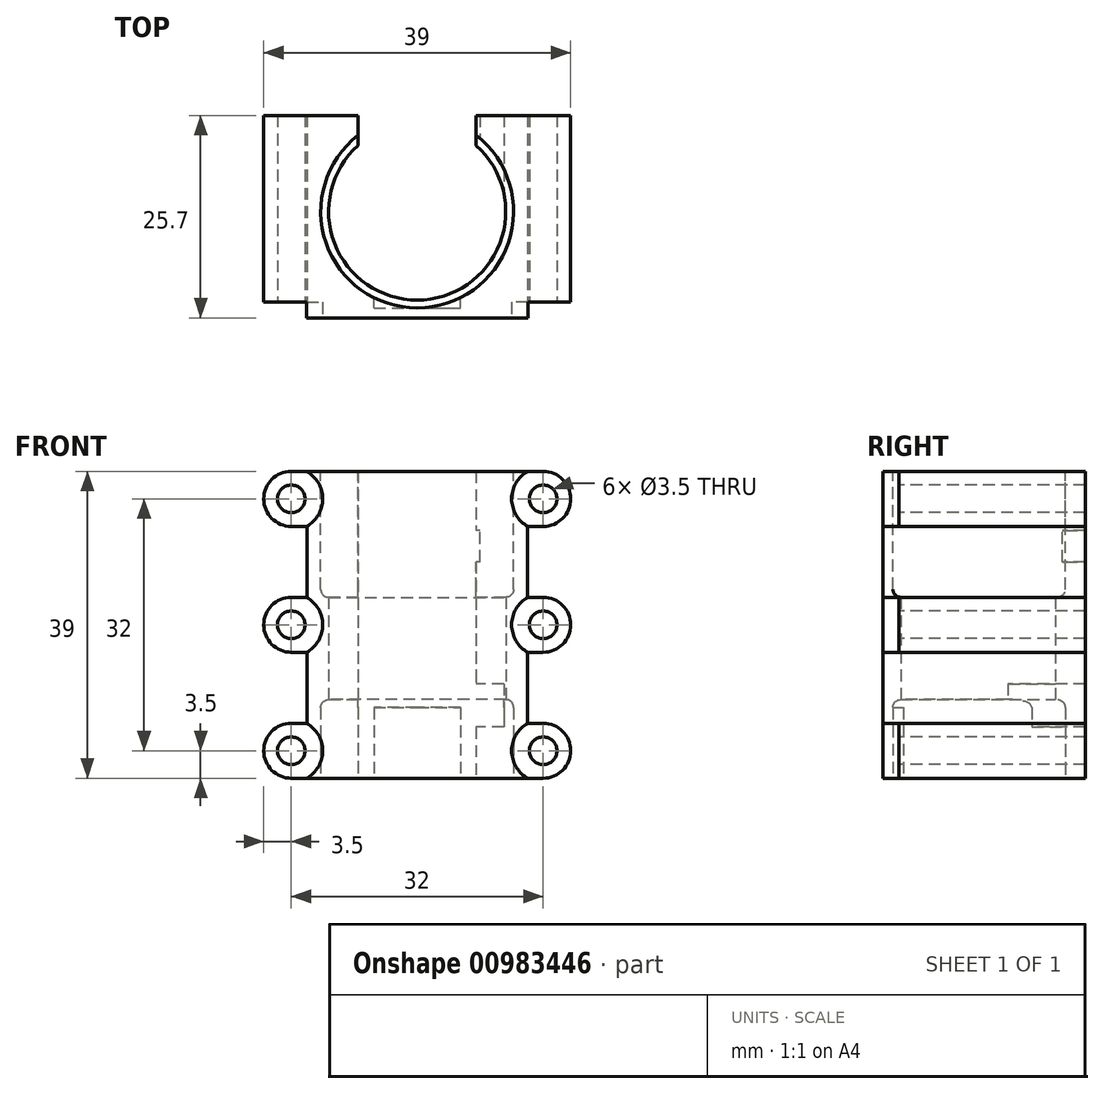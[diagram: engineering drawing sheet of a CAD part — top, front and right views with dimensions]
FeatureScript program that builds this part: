
annotation { "Feature Type Name" : "Feature", "Feature Type Description" : "" }
export const myFeature = defineFeature(function(context is Context, id is Id, definition is map)
    precondition{}
    {
        {
            var Q0;
            Q0=qCreatedBy(makeId("Top.planeOp"),FACE);
            var sketch = newSketch(context, id + "F0", { "sketchPlane" : qUnion([Q0])});
            skCircle(sketch, "E0", {"center": v(0, 0) * mm, "radius": 11.25 * mm});
            skSolve(sketch);
        }
        {
            var Q0;
            Q0=qSketchRegion(id+"F0",true);
            extrude(context, id + "F1", {"entities" : qUnion([Q0]), "depth" : 39 * mm, "offsetDistance" : 25 * mm});
        }
        {
            var Q0;
            Q0=makeQuery(id+"F1.opExtrude","CAP_FACE",FACE,{"disambiguationData":[OSD([sQuery(id+"F0.wireOp",EDGE,"E0")])],"isStart":false});
            var sketch = newSketch(context, id + "F2", { "sketchPlane" : qUnion([Q0])});
            skCircle(sketch, "E1", {"center": v(0, 0) * mm, "radius": 12.25 * mm});
            skSolve(sketch);
        }
        {
            var Q0;
            Q0=makeQuery(id+"F2.imprint","IMPRINT",FACE,{"disambiguationData":[TD([[makeQuery(id+"F2.imprint","IMPRINT",EDGE,{"derivedFrom":sQuery(id+"F2.wireOp",EDGE,"E1")}),1.0]])]});
            extrude(context, id + "F3", {"entities" : qUnion([Q0]), "operationType" : NewBodyOperationType.ADD, "oppositeDirection" : true, "depth" : 16 * mm, "offsetDistance" : 25 * mm});
        }
        {
            var Q0;
            Q0=makeQuery(id+"F1.opExtrude","CAP_FACE",FACE,{"disambiguationData":[OSD([sQuery(id+"F0.wireOp",EDGE,"E0")])],"isStart":true});
            var sketch = newSketch(context, id + "F4", { "sketchPlane" : qUnion([Q0])});
            skCircle(sketch, "E2", {"center": v(0, 0) * mm, "radius": 12.25 * mm});
            skSolve(sketch);
        }
        {
            var Q0;
            Q0=makeQuery(id+"F3.opExtrude","CAP_EDGE",EDGE,{"disambiguationData":[OSD([sQuery(id+"F2.wireOp",EDGE,"E1")])],"isStart":false});
            fillet(context, id + "F5", {"entities" : qUnion([Q0]), "radius" : 1 * mm, "tangentPropagation" : true, "allowEdgeOverflow" : false});
        }
        {
            var Q0;
            Q0=makeQuery(id+"F4.imprint","IMPRINT",FACE,{"disambiguationData":[TD([[makeQuery(id+"F4.imprint","IMPRINT",EDGE,{"derivedFrom":sQuery(id+"F4.wireOp",EDGE,"E2")}),1.0]])]});
            extrude(context, id + "F6", {"entities" : qUnion([Q0]), "operationType" : NewBodyOperationType.ADD, "oppositeDirection" : true, "depth" : 10 * mm, "offsetDistance" : 25 * mm});
        }
        {
            var Q0;
            Q0=makeQuery(id+"F6.opExtrude","CAP_EDGE",EDGE,{"disambiguationData":[OSD([sQuery(id+"F4.wireOp",EDGE,"E2")])],"isStart":false});
            fillet(context, id + "F7", {"entities" : qUnion([Q0]), "radius" : 1 * mm, "tangentPropagation" : true, "allowEdgeOverflow" : false});
        }
        {
            var Q0;
            {var subQ0=sQuery(id+"F0.wireOp",EDGE,"E0");Q0=makeQuery(id+"F6.boolean.opBoolean","MERGE",FACE,{"derivedFrom":[makeQuery(id+"F1.opExtrude","CAP_FACE",FACE,{"disambiguationData":[OSD([subQ0])],"isStart":true}),makeQuery(id+"F6.opExtrude","CAP_FACE",FACE,{"disambiguationData":[OSD([subQ0,sQuery(id+"F4.wireOp",EDGE,"E2")])],"isStart":true})]});}
            var sketch = newSketch(context, id + "F8", { "sketchPlane" : qUnion([Q0])});
            skLineSegment(sketch, "E3.bottom", {"start": v(-5.5, 12.25) * mm, "end": v(5.5, 12.25) * mm});
            skLineSegment(sketch, "E3.top", {"start": v(-5.5, 10.25) * mm, "end": v(5.5, 10.25) * mm});
            skLineSegment(sketch, "E3.left", {"start": v(-5.5, 12.25) * mm, "end": v(-5.5, 10.25) * mm});
            skLineSegment(sketch, "E3.right", {"start": v(5.5, 12.25) * mm, "end": v(5.5, 10.25) * mm});
            skPoint(sketch, "E3.middle", {"position": v(0, 11.25) * mm});
            skSolve(sketch);
        }
        {
            var Q0;
            {var subQ0=sQuery(id+"F8.wireOp",EDGE,"E3.left");var subQ1=sQuery(id+"F8.wireOp",EDGE,"E3.bottom");var subQ2=makeQuery(id+"F8.imprint","INTERSECT",VERTEX,{"derivedFrom":[subQ1,subQ0]});Q0=makeQuery(id+"F8.imprint","IMPRINT",FACE,{"disambiguationData":[TD([[makeQuery(id+"F8.imprint","IMPRINT",EDGE,{"disambiguationData":[TD([[subQ2,-1.0]])],"derivedFrom":subQ1}),-1.0]])]});}
            var Q1;
            {var subQ0=sQuery(id+"F8.wireOp",EDGE,"E3.right");var subQ1=sQuery(id+"F8.wireOp",EDGE,"E3.bottom");var subQ2=makeQuery(id+"F8.imprint","INTERSECT",VERTEX,{"derivedFrom":[subQ1,subQ0]});Q1=makeQuery(id+"F8.imprint","IMPRINT",FACE,{"disambiguationData":[TD([[makeQuery(id+"F8.imprint","IMPRINT",EDGE,{"disambiguationData":[TD([[subQ2,1.0]])],"derivedFrom":subQ1}),-1.0]])]});}
            extrude(context, id + "F9", {"entities" : qUnion([Q0, Q1]), "operationType" : NewBodyOperationType.ADD, "oppositeDirection" : true, "depth" : 9 * mm, "offsetDistance" : 25 * mm});
        }
        {
            var Q0;
            {var subQ0=sQuery(id+"F8.wireOp",EDGE,"E3.bottom");var subQ1=sQuery(id+"F4.wireOp",EDGE,"E2");var subQ2=sQuery(id+"F0.wireOp",EDGE,"E0");Q0=makeQuery(id+"F9.boolean.opBoolean","MERGE",FACE,{"derivedFrom":[makeQuery(id+"F6.boolean.opBoolean","MERGE",FACE,{"derivedFrom":[makeQuery(id+"F1.opExtrude","CAP_FACE",FACE,{"disambiguationData":[OSD([subQ2])],"isStart":true}),makeQuery(id+"F6.opExtrude","CAP_FACE",FACE,{"disambiguationData":[OSD([subQ2,subQ1])],"isStart":true})]}),makeQuery(id+"F9.opExtrude","CAP_FACE",FACE,{"disambiguationData":[OSD([subQ1,subQ0,sQuery(id+"F8.wireOp",EDGE,"E3.left")])],"isStart":true}),makeQuery(id+"F9.opExtrude","CAP_FACE",FACE,{"disambiguationData":[OSD([subQ1,subQ0,sQuery(id+"F8.wireOp",EDGE,"E3.right")])],"isStart":true})]});}
            var sketch = newSketch(context, id + "F10", { "sketchPlane" : qUnion([Q0])});
            skLineSegment(sketch, "E4.bottom", {"start": v(-7.5, -8.25) * mm, "end": v(7.5, -8.25) * mm});
            skLineSegment(sketch, "E4.top", {"start": v(-7.5, -12.25) * mm, "end": v(7.5, -12.25) * mm});
            skLineSegment(sketch, "E4.left", {"start": v(-7.5, -8.25) * mm, "end": v(-7.5, -12.25) * mm});
            skLineSegment(sketch, "E4.right", {"start": v(7.5, -8.25) * mm, "end": v(7.5, -12.25) * mm});
            skPoint(sketch, "E4.middle", {"position": v(0, -10.25) * mm});
            skSolve(sketch);
        }
        {
            var Q0;
            {var subQ0=sQuery(id+"F10.wireOp",EDGE,"E4.right");var subQ1=sQuery(id+"F10.wireOp",EDGE,"E4.top");var subQ2=makeQuery(id+"F10.imprint","INTERSECT",VERTEX,{"derivedFrom":[subQ1,subQ0]});Q0=makeQuery(id+"F10.imprint","IMPRINT",FACE,{"disambiguationData":[TD([[makeQuery(id+"F10.imprint","IMPRINT",EDGE,{"disambiguationData":[TD([[subQ2,1.0]])],"derivedFrom":subQ1}),1.0]])]});}
            var Q1;
            {var subQ0=sQuery(id+"F10.wireOp",EDGE,"E4.left");var subQ1=sQuery(id+"F10.wireOp",EDGE,"E4.top");var subQ2=makeQuery(id+"F10.imprint","INTERSECT",VERTEX,{"derivedFrom":[subQ1,subQ0]});Q1=makeQuery(id+"F10.imprint","IMPRINT",FACE,{"disambiguationData":[TD([[makeQuery(id+"F10.imprint","IMPRINT",EDGE,{"disambiguationData":[TD([[subQ2,-1.0]])],"derivedFrom":subQ1}),1.0]])]});}
            var Q2;
            {var subQ4=sQuery(id+"F10.wireOp",EDGE,"E4.bottom");Q2=makeQuery(id+"F10.imprint","IMPRINT",FACE,{"disambiguationData":[TD([[makeQuery(id+"F10.imprint","IMPRINT",EDGE,{"derivedFrom":subQ4}),-1.0]])]});}
            extrude(context, id + "F11", {"entities" : qUnion([Q0, Q1, Q2]), "operationType" : NewBodyOperationType.ADD, "oppositeDirection" : true, "depth" : 39 * mm, "offsetDistance" : 25 * mm});
        }
        {
            var Q0;
            Q0=makeQuery(id+"F11.opExtrude","SWEPT_FACE",FACE,{"disambiguationData":[OSD([sQuery(id+"F10.wireOp",EDGE,"E4.top")])]});
            var sketch = newSketch(context, id + "F12", { "sketchPlane" : qUnion([Q0])});
            skLineSegment(sketch, "E5.bottom", {"start": v(-11, 12) * mm, "end": v(-7.5, 12) * mm});
            skLineSegment(sketch, "E5.top", {"start": v(-11, 6.5) * mm, "end": v(-7.5, 6.5) * mm});
            skLineSegment(sketch, "E5.left", {"start": v(-11, 12) * mm, "end": v(-11, 6.5) * mm});
            skLineSegment(sketch, "E5.right", {"start": v(-7.5, 12) * mm, "end": v(-7.5, 6.5) * mm});
            skSolve(sketch);
        }
        {
            var Q0;
            Q0=makeQuery(id+"F12.imprint","IMPRINT",FACE,{"disambiguationData":[TD([[makeQuery(id+"F12.imprint","IMPRINT",EDGE,{"derivedFrom":sQuery(id+"F12.wireOp",EDGE,"E5.bottom")}),-1.0]])]});
            extrude(context, id + "F13", {"entities" : qUnion([Q0]), "operationType" : NewBodyOperationType.ADD, "depth" : 2 * mm, "offsetDistance" : 25 * mm, "hasSecondDirection" : true, "secondDirectionOppositeDirection" : true, "secondDirectionDepth" : 12 * mm});
        }
        {
            var Q0;
            Q0=makeQuery(id+"F11.opExtrude","SWEPT_FACE",FACE,{"disambiguationData":[OSD([sQuery(id+"F10.wireOp",EDGE,"E4.top")])]});
            var sketch = newSketch(context, id + "F14", { "sketchPlane" : qUnion([Q0])});
            skCircle(sketch, "E6", {"center": v(-0.06, 19) * mm, "radius": 6.5 * mm});
            skSolve(sketch);
        }
        {
            var Q0;
            Q0=makeQuery(id+"F14.imprint","IMPRINT",FACE,{"disambiguationData":[TD([[makeQuery(id+"F14.imprint","IMPRINT",EDGE,{"derivedFrom":sQuery(id+"F14.wireOp",EDGE,"E6")}),1.0]])]});
            extrude(context, id + "F15", {"entities" : qUnion([Q0]), "operationType" : NewBodyOperationType.ADD, "depth" : 2 * mm, "offsetDistance" : 25 * mm});
        }
        {
            var Q0;
            Q0=makeQuery(id+"F11.opExtrude","SWEPT_FACE",FACE,{"disambiguationData":[OSD([sQuery(id+"F10.wireOp",EDGE,"E4.top")])]});
            var sketch = newSketch(context, id + "F16", { "sketchPlane" : qUnion([Q0])});
            skLineSegment(sketch, "E7.bottom", {"start": v(-8, 27.5) * mm, "end": v(-4.5, 27.5) * mm});
            skLineSegment(sketch, "E7.top", {"start": v(-8, 31.5) * mm, "end": v(-4.5, 31.5) * mm});
            skLineSegment(sketch, "E7.left", {"start": v(-8, 27.5) * mm, "end": v(-8, 31.5) * mm});
            skLineSegment(sketch, "E7.right", {"start": v(-4.5, 27.5) * mm, "end": v(-4.5, 31.5) * mm});
            skSolve(sketch);
        }
        {
            var Q0;
            Q0=makeQuery(id+"F16.imprint","IMPRINT",FACE,{"disambiguationData":[TD([[makeQuery(id+"F16.imprint","IMPRINT",EDGE,{"derivedFrom":sQuery(id+"F16.wireOp",EDGE,"E7.bottom")}),1.0]])]});
            var Q1;
            {var subQ2=sQuery(id+"F16.wireOp",EDGE,"E7.right");Q1=makeQuery(id+"F16.imprint","IMPRINT",FACE,{"disambiguationData":[TD([[makeQuery(id+"F16.imprint","IMPRINT",EDGE,{"derivedFrom":subQ2}),1.0]])]});}
            extrude(context, id + "F17", {"entities" : qUnion([Q0, Q1]), "operationType" : NewBodyOperationType.ADD, "depth" : 6 * mm, "offsetDistance" : 25 * mm, "hasSecondDirection" : true, "secondDirectionOppositeDirection" : true, "secondDirectionDepth" : 16.7 * mm});
        }
        {
            var Q0;
            Q0=qCreatedBy(makeId("Front.planeOp"),FACE);
            var sketch = newSketch(context, id + "F18", { "sketchPlane" : qUnion([Q0])});
            skLineSegment(sketch, "E8.bottom", {"start": v(14, 0) * mm, "end": v(-14, 0) * mm});
            skLineSegment(sketch, "E8.top", {"start": v(14, 39) * mm, "end": v(-14, 39) * mm});
            skLineSegment(sketch, "E8.left", {"start": v(14, 0) * mm, "end": v(14, 39) * mm});
            skLineSegment(sketch, "E8.right", {"start": v(-14, 0) * mm, "end": v(-14, 39) * mm});
            skPoint(sketch, "E8.middle", {"position": v(0, 19.5) * mm});
            skSolve(sketch);
        }
        {
            var Q0;
            Q0=makeQuery(id+"F18.imprint","IMPRINT",FACE,{"disambiguationData":[TD([[makeQuery(id+"F18.imprint","IMPRINT",EDGE,{"derivedFrom":sQuery(id+"F18.wireOp",EDGE,"E8.bottom")}),-1.0]])]});
            extrude(context, id + "F19", {"entities" : qUnion([Q0]), "depth" : 13.5 * mm, "offsetDistance" : 25 * mm, "hasSecondDirection" : true, "secondDirectionOppositeDirection" : true, "secondDirectionDepth" : 12.2 * mm});
        }
        {
            var Q0;
            Q0=makeQuery(id+"F1.opExtrude","SWEPT_BODY",BODY,{"disambiguationData":[OSD([sQuery(id+"F0.wireOp",EDGE,"E0")])]});
            var Q1;
            Q1=makeQuery(id+"F19.opExtrude","SWEPT_BODY",BODY,{"disambiguationData":[OSD([sQuery(id+"F18.wireOp",EDGE,"E8.bottom"),sQuery(id+"F18.wireOp",EDGE,"E8.top"),sQuery(id+"F18.wireOp",EDGE,"E8.left"),sQuery(id+"F18.wireOp",EDGE,"E8.right")])]});
            booleanBodies(context, id + "F20", {"operationType" : BooleanOperationType.SUBTRACTION, "tools" : qUnion([Q0]), "targets" : qUnion([Q1])});
        }
        {
            var Q0;
            Q0=makeQuery(id+"F19.opExtrude","CAP_FACE",FACE,{"disambiguationData":[OSD([sQuery(id+"F18.wireOp",EDGE,"E8.bottom"),sQuery(id+"F18.wireOp",EDGE,"E8.top"),sQuery(id+"F18.wireOp",EDGE,"E8.left"),sQuery(id+"F18.wireOp",EDGE,"E8.right")])],"isStart":false});
            var sketch = newSketch(context, id + "F21", { "sketchPlane" : qUnion([Q0])});
            skLineSegment(sketch, "E9.bottom", {"start": v(16, 7) * mm, "end": v(-16, 7) * mm});
            skLineSegment(sketch, "E9.top", {"start": v(16, 0) * mm, "end": v(-16, 0) * mm});
            skLineSegment(sketch, "E9.left", {"start": v(19.5, 3.5) * mm, "end": v(19.5, 3.5) * mm});
            skLineSegment(sketch, "E9.right", {"start": v(-19.5, 3.5) * mm, "end": v(-19.5, 3.5) * mm});
            skPoint(sketch, "E9.middle", {"position": v(0, 3.5) * mm});
            skLineSegment(sketch, "E10.bottom", {"start": v(16, 39) * mm, "end": v(-16, 39) * mm});
            skLineSegment(sketch, "E10.top", {"start": v(16, 32) * mm, "end": v(-16, 32) * mm});
            skLineSegment(sketch, "E10.left", {"start": v(19.5, 35.5) * mm, "end": v(19.5, 35.5) * mm});
            skLineSegment(sketch, "E10.right", {"start": v(-19.5, 35.5) * mm, "end": v(-19.5, 35.5) * mm});
            skPoint(sketch, "E10.middle", {"position": v(0, 35.5) * mm});
            skPoint(sketch, "E11.visualSharp", {"position": v(-19.5, 0) * mm});
            skArc(sketch, "E11.filletArc", {"start": v(-19.5, 3.5) * mm, "mid": v(-18.47, 1.03) * mm, "end": v(-16, 0) * mm});
            skPoint(sketch, "E12.visualSharp", {"position": v(-19.5, 7) * mm});
            skArc(sketch, "E12.filletArc", {"start": v(-16, 7) * mm, "mid": v(-18.47, 5.97) * mm, "end": v(-19.5, 3.5) * mm});
            skPoint(sketch, "E13.visualSharp", {"position": v(-19.5, 32) * mm});
            skArc(sketch, "E13.filletArc", {"start": v(-19.5, 35.5) * mm, "mid": v(-18.47, 33.03) * mm, "end": v(-16, 32) * mm});
            skPoint(sketch, "E14.visualSharp", {"position": v(19.5, 39) * mm});
            skArc(sketch, "E14.filletArc", {"start": v(19.5, 35.5) * mm, "mid": v(18.47, 37.97) * mm, "end": v(16, 39) * mm});
            skPoint(sketch, "E15.visualSharp", {"position": v(19.5, 32) * mm});
            skArc(sketch, "E15.filletArc", {"start": v(16, 32) * mm, "mid": v(18.47, 33.03) * mm, "end": v(19.5, 35.5) * mm});
            skPoint(sketch, "E16.visualSharp", {"position": v(19.5, 0) * mm});
            skArc(sketch, "E16.filletArc", {"start": v(16, 0) * mm, "mid": v(18.47, 1.03) * mm, "end": v(19.5, 3.5) * mm});
            skPoint(sketch, "E17.visualSharp", {"position": v(-19.5, 39) * mm});
            skArc(sketch, "E17.filletArc", {"start": v(-16, 39) * mm, "mid": v(-18.47, 37.97) * mm, "end": v(-19.5, 35.5) * mm});
            skPoint(sketch, "E18.visualSharp", {"position": v(19.5, 7) * mm});
            skArc(sketch, "E18.filletArc", {"start": v(19.5, 3.5) * mm, "mid": v(18.47, 5.97) * mm, "end": v(16, 7) * mm});
            skCircle(sketch, "E19", {"center": v(-16, 35.5) * mm, "radius": 1.75 * mm});
            skCircle(sketch, "E20", {"center": v(16, 35.5) * mm, "radius": 1.75 * mm});
            skCircle(sketch, "E21", {"center": v(16, 3.5) * mm, "radius": 1.75 * mm});
            skCircle(sketch, "E22", {"center": v(-16, 3.5) * mm, "radius": 1.75 * mm});
            skLineSegment(sketch, "E23.bottom", {"start": v(16, 16) * mm, "end": v(-16, 16) * mm});
            skLineSegment(sketch, "E23.top", {"start": v(16, 23) * mm, "end": v(-16, 23) * mm});
            skLineSegment(sketch, "E23.left", {"start": v(19.5, 19.5) * mm, "end": v(19.5, 19.5) * mm});
            skLineSegment(sketch, "E23.right", {"start": v(-19.5, 19.5) * mm, "end": v(-19.5, 19.5) * mm});
            skPoint(sketch, "E23.middle", {"position": v(0, 19.5) * mm});
            skPoint(sketch, "E24.visualSharp", {"position": v(-19.5, 23) * mm});
            skArc(sketch, "E24.filletArc", {"start": v(-16, 23) * mm, "mid": v(-18.47, 21.97) * mm, "end": v(-19.5, 19.5) * mm});
            skPoint(sketch, "E25.visualSharp", {"position": v(-19.5, 16) * mm});
            skArc(sketch, "E25.filletArc", {"start": v(-19.5, 19.5) * mm, "mid": v(-18.47, 17.03) * mm, "end": v(-16, 16) * mm});
            skPoint(sketch, "E26.visualSharp", {"position": v(19.5, 16) * mm});
            skArc(sketch, "E26.filletArc", {"start": v(16, 16) * mm, "mid": v(18.47, 17.03) * mm, "end": v(19.5, 19.5) * mm});
            skPoint(sketch, "E27.visualSharp", {"position": v(19.5, 23) * mm});
            skArc(sketch, "E27.filletArc", {"start": v(19.5, 19.5) * mm, "mid": v(18.47, 21.97) * mm, "end": v(16, 23) * mm});
            skCircle(sketch, "E28", {"center": v(-16, 19.5) * mm, "radius": 1.75 * mm});
            skCircle(sketch, "E29", {"center": v(16, 19.5) * mm, "radius": 1.75 * mm});
            skSolve(sketch);
        }
        {
            var Q0;
            {var subQ0=sQuery(id+"F21.wireOp",EDGE,"E11.filletArc");Q0=makeQuery(id+"F21.imprint","IMPRINT",FACE,{"disambiguationData":[TD([[makeQuery(id+"F21.imprint","IMPRINT",EDGE,{"derivedFrom":subQ0}),1.0]])]});}
            var Q1;
            {var subQ5=sQuery(id+"F21.wireOp",EDGE,"E13.filletArc");Q1=makeQuery(id+"F21.imprint","IMPRINT",FACE,{"disambiguationData":[TD([[makeQuery(id+"F21.imprint","IMPRINT",EDGE,{"derivedFrom":subQ5}),1.0]])]});}
            var Q2;
            {var subQ5=sQuery(id+"F21.wireOp",EDGE,"E14.filletArc");Q2=makeQuery(id+"F21.imprint","IMPRINT",FACE,{"disambiguationData":[TD([[makeQuery(id+"F21.imprint","IMPRINT",EDGE,{"derivedFrom":subQ5}),1.0]])]});}
            var Q3;
            {var subQ4=sQuery(id+"F21.wireOp",EDGE,"E16.filletArc");Q3=makeQuery(id+"F21.imprint","IMPRINT",FACE,{"disambiguationData":[TD([[makeQuery(id+"F21.imprint","IMPRINT",EDGE,{"derivedFrom":subQ4}),1.0]])]});}
            var Q4;
            {var subQ4=sQuery(id+"F21.wireOp",EDGE,"E24.filletArc");var subQ6=sQuery(id+"F21.wireOp",EDGE,"E25.filletArc");var subQ7=makeQuery(id+"F21.imprint","INTERSECT",VERTEX,{"derivedFrom":[subQ4,subQ6]});Q4=makeQuery(id+"F21.imprint","IMPRINT",FACE,{"disambiguationData":[TD([[makeQuery(id+"F21.imprint","IMPRINT",EDGE,{"disambiguationData":[TD([[subQ7,1.0]])],"derivedFrom":subQ4}),1.0]])]});}
            var Q5;
            {var subQ0=sQuery(id+"F21.wireOp",EDGE,"E26.filletArc");var subQ6=sQuery(id+"F21.wireOp",EDGE,"E27.filletArc");var subQ7=makeQuery(id+"F21.imprint","INTERSECT",VERTEX,{"derivedFrom":[subQ0,subQ6]});Q5=makeQuery(id+"F21.imprint","IMPRINT",FACE,{"disambiguationData":[TD([[makeQuery(id+"F21.imprint","IMPRINT",EDGE,{"disambiguationData":[TD([[subQ7,1.0]])],"derivedFrom":subQ0}),1.0]])]});}
            extrude(context, id + "F22", {"entities" : qUnion([Q0, Q1, Q2, Q3, Q4, Q5]), "operationType" : NewBodyOperationType.ADD, "oppositeDirection" : true, "depth" : 25.7 * mm, "offsetDistance" : 25 * mm});
        }
        {
            var Q0;
            {var subQ0=sQuery(id+"F21.wireOp",EDGE,"E22");var subQ1=makeQuery(id+"F19.opExtrude","CAP_EDGE",EDGE,{"disambiguationData":[OSD([sQuery(id+"F18.wireOp",EDGE,"E8.right")])],"isStart":false});var subQ2=makeQuery(id+"F21.imprint","INTERSECT",VERTEX,{"disambiguationData":[OD(0.0)],"derivedFrom":[subQ1,subQ0]});Q0=makeQuery(id+"F21.imprint","IMPRINT",FACE,{"disambiguationData":[TD([[makeQuery(id+"F21.imprint","IMPRINT",EDGE,{"disambiguationData":[TD([[subQ2,-1.0]])],"derivedFrom":subQ0}),1.0]])]});}
            var Q1;
            {var subQ0=sQuery(id+"F21.wireOp",EDGE,"E21");var subQ1=makeQuery(id+"F19.opExtrude","CAP_EDGE",EDGE,{"disambiguationData":[OSD([sQuery(id+"F18.wireOp",EDGE,"E8.left")])],"isStart":false});var subQ2=makeQuery(id+"F21.imprint","INTERSECT",VERTEX,{"disambiguationData":[OD(0.0)],"derivedFrom":[subQ1,subQ0]});Q1=makeQuery(id+"F21.imprint","IMPRINT",FACE,{"disambiguationData":[TD([[makeQuery(id+"F21.imprint","IMPRINT",EDGE,{"disambiguationData":[TD([[subQ2,1.0]])],"derivedFrom":subQ0}),1.0]])]});}
            var Q2;
            {var subQ0=sQuery(id+"F21.wireOp",EDGE,"E20");var subQ1=makeQuery(id+"F19.opExtrude","CAP_EDGE",EDGE,{"disambiguationData":[OSD([sQuery(id+"F18.wireOp",EDGE,"E8.left")])],"isStart":false});var subQ2=makeQuery(id+"F21.imprint","INTERSECT",VERTEX,{"disambiguationData":[OD(0.0)],"derivedFrom":[subQ1,subQ0]});Q2=makeQuery(id+"F21.imprint","IMPRINT",FACE,{"disambiguationData":[TD([[makeQuery(id+"F21.imprint","IMPRINT",EDGE,{"disambiguationData":[TD([[subQ2,-1.0]])],"derivedFrom":subQ0}),1.0]])]});}
            var Q3;
            {var subQ0=sQuery(id+"F21.wireOp",EDGE,"E19");var subQ1=makeQuery(id+"F19.opExtrude","CAP_EDGE",EDGE,{"disambiguationData":[OSD([sQuery(id+"F18.wireOp",EDGE,"E8.right")])],"isStart":false});var subQ2=makeQuery(id+"F21.imprint","INTERSECT",VERTEX,{"disambiguationData":[OD(0.0)],"derivedFrom":[subQ1,subQ0]});Q3=makeQuery(id+"F21.imprint","IMPRINT",FACE,{"disambiguationData":[TD([[makeQuery(id+"F21.imprint","IMPRINT",EDGE,{"disambiguationData":[TD([[subQ2,1.0]])],"derivedFrom":subQ0}),1.0]])]});}
            var Q4;
            {var subQ0=sQuery(id+"F21.wireOp",EDGE,"E19");var subQ1=makeQuery(id+"F19.opExtrude","CAP_EDGE",EDGE,{"disambiguationData":[OSD([sQuery(id+"F18.wireOp",EDGE,"E8.right")])],"isStart":false});var subQ2=makeQuery(id+"F21.imprint","INTERSECT",VERTEX,{"disambiguationData":[OD(0.0)],"derivedFrom":[subQ1,subQ0]});Q4=makeQuery(id+"F21.imprint","IMPRINT",FACE,{"disambiguationData":[TD([[makeQuery(id+"F21.imprint","IMPRINT",EDGE,{"disambiguationData":[TD([[subQ2,-1.0]])],"derivedFrom":subQ0}),1.0]])]});}
            var Q5;
            {var subQ0=sQuery(id+"F21.wireOp",EDGE,"E28");var subQ1=makeQuery(id+"F19.opExtrude","CAP_EDGE",EDGE,{"disambiguationData":[OSD([sQuery(id+"F18.wireOp",EDGE,"E8.right")])],"isStart":false});var subQ2=makeQuery(id+"F21.imprint","INTERSECT",VERTEX,{"disambiguationData":[OD(0.0)],"derivedFrom":[subQ1,subQ0]});Q5=makeQuery(id+"F21.imprint","IMPRINT",FACE,{"disambiguationData":[TD([[makeQuery(id+"F21.imprint","IMPRINT",EDGE,{"disambiguationData":[TD([[subQ2,1.0]])],"derivedFrom":subQ0}),1.0]])]});}
            var Q6;
            {var subQ0=sQuery(id+"F21.wireOp",EDGE,"E29");var subQ1=makeQuery(id+"F19.opExtrude","CAP_EDGE",EDGE,{"disambiguationData":[OSD([sQuery(id+"F18.wireOp",EDGE,"E8.left")])],"isStart":false});var subQ2=makeQuery(id+"F21.imprint","INTERSECT",VERTEX,{"disambiguationData":[OD(0.0)],"derivedFrom":[subQ1,subQ0]});Q6=makeQuery(id+"F21.imprint","IMPRINT",FACE,{"disambiguationData":[TD([[makeQuery(id+"F21.imprint","IMPRINT",EDGE,{"disambiguationData":[TD([[subQ2,1.0]])],"derivedFrom":subQ0}),1.0]])]});}
            var Q7;
            {var subQ0=sQuery(id+"F21.wireOp",EDGE,"E28");var subQ1=makeQuery(id+"F19.opExtrude","CAP_EDGE",EDGE,{"disambiguationData":[OSD([sQuery(id+"F18.wireOp",EDGE,"E8.right")])],"isStart":false});var subQ2=makeQuery(id+"F21.imprint","INTERSECT",VERTEX,{"disambiguationData":[OD(0.0)],"derivedFrom":[subQ1,subQ0]});Q7=makeQuery(id+"F21.imprint","IMPRINT",FACE,{"disambiguationData":[TD([[makeQuery(id+"F21.imprint","IMPRINT",EDGE,{"disambiguationData":[TD([[subQ2,-1.0]])],"derivedFrom":subQ0}),1.0]])]});}
            extrude(context, id + "F23", {"entities" : qUnion([Q0, Q1, Q2, Q3, Q4, Q5, Q6, Q7]), "operationType" : NewBodyOperationType.REMOVE, "oppositeDirection" : true, "depth" : 25.7 * mm, "offsetDistance" : 25 * mm});
        }
        {
            var Q0;
            {var subQ0=sQuery(id+"F18.wireOp",EDGE,"E8.left");var subQ1=sQuery(id+"F18.wireOp",EDGE,"E8.right");Q0=makeQuery(id+"F22.boolean.opBoolean","MERGE",FACE,{"derivedFrom":[makeQuery(id+"F19.opExtrude","CAP_FACE",FACE,{"disambiguationData":[OSD([sQuery(id+"F18.wireOp",EDGE,"E8.bottom"),sQuery(id+"F18.wireOp",EDGE,"E8.top"),subQ0,subQ1])],"isStart":false}),makeQuery(id+"F22.opExtrude","CAP_FACE",FACE,{"disambiguationData":[OSD([subQ1,sQuery(id+"F21.wireOp",EDGE,"E11.filletArc"),sQuery(id+"F21.wireOp",EDGE,"E12.filletArc"),sQuery(id+"F21.wireOp",EDGE,"E22")])],"isStart":true}),makeQuery(id+"F22.opExtrude","CAP_FACE",FACE,{"disambiguationData":[OSD([subQ1,sQuery(id+"F21.wireOp",EDGE,"E13.filletArc"),sQuery(id+"F21.wireOp",EDGE,"E17.filletArc"),sQuery(id+"F21.wireOp",EDGE,"E19")])],"isStart":true}),makeQuery(id+"F22.opExtrude","CAP_FACE",FACE,{"disambiguationData":[OSD([subQ0,sQuery(id+"F21.wireOp",EDGE,"E14.filletArc"),sQuery(id+"F21.wireOp",EDGE,"E15.filletArc"),sQuery(id+"F21.wireOp",EDGE,"E20")])],"isStart":true}),makeQuery(id+"F22.opExtrude","CAP_FACE",FACE,{"disambiguationData":[OSD([subQ0,sQuery(id+"F21.wireOp",EDGE,"E16.filletArc"),sQuery(id+"F21.wireOp",EDGE,"E18.filletArc"),sQuery(id+"F21.wireOp",EDGE,"E21")])],"isStart":true})]});}
            var sketch = newSketch(context, id + "F24", { "sketchPlane" : qUnion([Q0])});
            skCircle(sketch, "E30", {"center": v(-16, 35.5) * mm, "radius": 4 * mm});
            skCircle(sketch, "E31", {"center": v(16, 35.5) * mm, "radius": 4 * mm});
            skCircle(sketch, "E32", {"center": v(16, 3.5) * mm, "radius": 4 * mm});
            skCircle(sketch, "E33", {"center": v(-16, 3.5) * mm, "radius": 4 * mm});
            skCircle(sketch, "E34", {"center": v(-16, 19.5) * mm, "radius": 4 * mm});
            skCircle(sketch, "E35", {"center": v(16, 19.5) * mm, "radius": 4 * mm});
            skSolve(sketch);
        }
        {
            var Q0;
            {var subQ9=sQuery(id+"F21.wireOp",EDGE,"E19");Q0=makeQuery(id+"F24.imprint","IMPRINT",FACE,{"disambiguationData":[TD([[makeQuery(id+"F24.imprint","IMPRINT",EDGE,{"derivedFrom":makeQuery(id+"F23.boolean.opBoolean","MERGE",EDGE,{"derivedFrom":[makeQuery(id+"F22.opExtrude","CAP_EDGE",EDGE,{"disambiguationData":[OSD([subQ9])],"isStart":true})],"fromTools":[makeQuery(id+"F23.opExtrude","CAP_EDGE",EDGE,{"disambiguationData":[OSD([subQ9])],"isStart":true})]})}),-1.0]])]});}
            var Q1;
            {var subQ7=sQuery(id+"F21.wireOp",EDGE,"E20");Q1=makeQuery(id+"F24.imprint","IMPRINT",FACE,{"disambiguationData":[TD([[makeQuery(id+"F24.imprint","IMPRINT",EDGE,{"derivedFrom":makeQuery(id+"F23.boolean.opBoolean","MERGE",EDGE,{"derivedFrom":[makeQuery(id+"F22.opExtrude","CAP_EDGE",EDGE,{"disambiguationData":[OSD([subQ7])],"isStart":true})],"fromTools":[makeQuery(id+"F23.opExtrude","CAP_EDGE",EDGE,{"disambiguationData":[OSD([subQ7])],"isStart":true})]})}),-1.0]])]});}
            var Q2;
            {var subQ9=sQuery(id+"F21.wireOp",EDGE,"E21");Q2=makeQuery(id+"F24.imprint","IMPRINT",FACE,{"disambiguationData":[TD([[makeQuery(id+"F24.imprint","IMPRINT",EDGE,{"derivedFrom":makeQuery(id+"F23.boolean.opBoolean","MERGE",EDGE,{"derivedFrom":[makeQuery(id+"F22.opExtrude","CAP_EDGE",EDGE,{"disambiguationData":[OSD([subQ9])],"isStart":true})],"fromTools":[makeQuery(id+"F23.opExtrude","CAP_EDGE",EDGE,{"disambiguationData":[OSD([subQ9])],"isStart":true})]})}),-1.0]])]});}
            var Q3;
            {var subQ9=sQuery(id+"F21.wireOp",EDGE,"E22");Q3=makeQuery(id+"F24.imprint","IMPRINT",FACE,{"disambiguationData":[TD([[makeQuery(id+"F24.imprint","IMPRINT",EDGE,{"derivedFrom":makeQuery(id+"F23.boolean.opBoolean","MERGE",EDGE,{"derivedFrom":[makeQuery(id+"F22.opExtrude","CAP_EDGE",EDGE,{"disambiguationData":[OSD([subQ9])],"isStart":true})],"fromTools":[makeQuery(id+"F23.opExtrude","CAP_EDGE",EDGE,{"disambiguationData":[OSD([subQ9])],"isStart":true})]})}),-1.0]])]});}
            var Q4;
            {var subQ6=sQuery(id+"F21.wireOp",EDGE,"E28");Q4=makeQuery(id+"F24.imprint","IMPRINT",FACE,{"disambiguationData":[TD([[makeQuery(id+"F24.imprint","IMPRINT",EDGE,{"derivedFrom":makeQuery(id+"F23.boolean.opBoolean","MERGE",EDGE,{"derivedFrom":[makeQuery(id+"F22.opExtrude","CAP_EDGE",EDGE,{"disambiguationData":[OSD([subQ6])],"isStart":true})],"fromTools":[makeQuery(id+"F23.opExtrude","CAP_EDGE",EDGE,{"disambiguationData":[OSD([subQ6])],"isStart":true})]})}),-1.0]])]});}
            var Q5;
            {var subQ6=sQuery(id+"F21.wireOp",EDGE,"E29");Q5=makeQuery(id+"F24.imprint","IMPRINT",FACE,{"disambiguationData":[TD([[makeQuery(id+"F24.imprint","IMPRINT",EDGE,{"derivedFrom":makeQuery(id+"F23.boolean.opBoolean","MERGE",EDGE,{"derivedFrom":[makeQuery(id+"F22.opExtrude","CAP_EDGE",EDGE,{"disambiguationData":[OSD([subQ6])],"isStart":true})],"fromTools":[makeQuery(id+"F23.opExtrude","CAP_EDGE",EDGE,{"disambiguationData":[OSD([subQ6])],"isStart":true})]})}),-1.0]])]});}
            extrude(context, id + "F25", {"entities" : qUnion([Q0, Q1, Q2, Q3, Q4, Q5]), "operationType" : NewBodyOperationType.REMOVE, "oppositeDirection" : true, "depth" : 2 * mm, "offsetDistance" : 25 * mm});
        }
    });
